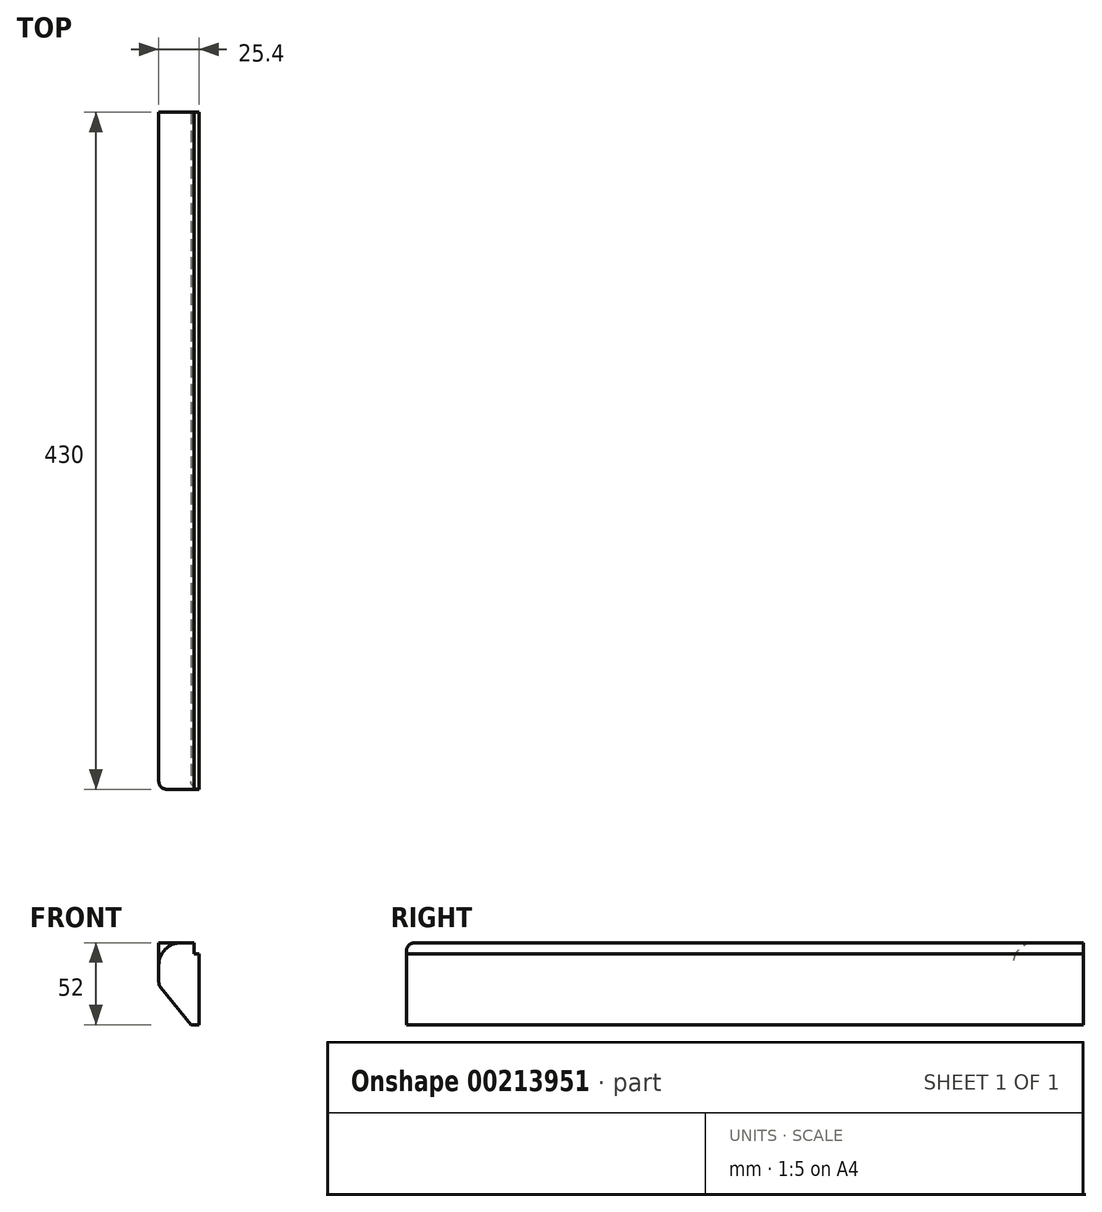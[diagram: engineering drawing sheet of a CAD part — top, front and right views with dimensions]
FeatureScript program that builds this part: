
annotation { "Feature Type Name" : "Feature", "Feature Type Description" : "" }
export const myFeature = defineFeature(function(context is Context, id is Id, definition is map)
    precondition{}
    {
        {
            var Q0;
            Q0=qCreatedBy(makeId("Front.planeOp"),FACE);
            var sketch = newSketch(context, id + "F0", { "sketchPlane" : qUnion([Q0])});
            skLineSegment(sketch, "E0.bottom", {"start": v(-25.49, -0.03) * mm, "end": v(-3.09, -0.03) * mm});
            skLineSegment(sketch, "E0.top", {"start": v(-5.09, -52.03) * mm, "end": v(-0.09, -52.03) * mm});
            skLineSegment(sketch, "E0.left", {"start": v(-25.49, -0.03) * mm, "end": v(-25.49, -25.25) * mm});
            skLineSegment(sketch, "E0.right", {"start": v(-0.09, -7.03) * mm, "end": v(-0.09, -52.03) * mm});
            skLineSegment(sketch, "E1", {"start": v(-24.36, -28.41) * mm, "end": v(-5.09, -52.03) * mm});
            skPoint(sketch, "E2.visualSharp", {"position": v(-25.49, -0.03) * mm});
            skPoint(sketch, "E3.visualSharp", {"position": v(-25.49, -27.03) * mm});
            skArc(sketch, "E3.filletArc", {"start": v(-25.49, -25.25) * mm, "mid": v(-25.2, -26.93) * mm, "end": v(-24.36, -28.41) * mm});
            skLineSegment(sketch, "E4.top", {"start": v(-3.09, -7.03) * mm, "end": v(-0.09, -7.03) * mm});
            skLineSegment(sketch, "E4.left", {"start": v(-3.09, -0.03) * mm, "end": v(-3.09, -7.03) * mm});
            skPoint(sketch, "E5.orphan", {"position": v(-0.09, -0.03) * mm});
            skSolve(sketch);
        }
        {
            var Q0;
            Q0 = qSketchRegion(id + "F0", true);
            extrude(context, id + "F1", {"entities" : qUnion([Q0]), "oppositeDirection" : true, "depth" : 430 * mm});
        }
        {
            var Q0;
            Q0=makeQuery(id+"F1.opExtrude","CAP_FACE",FACE,{"disambiguationData":[OSD([sQuery(id+"F0.wireOp",EDGE,"E0.bottom"),sQuery(id+"F0.wireOp",EDGE,"E0.top"),sQuery(id+"F0.wireOp",EDGE,"E0.left"),sQuery(id+"F0.wireOp",EDGE,"E0.right"),sQuery(id+"F0.wireOp",EDGE,"E1"),sQuery(id+"F0.wireOp",EDGE,"E3.filletArc")])],"isStart":false});
            cPlane(context, id + "F2", {"entities" : qUnion([Q0]), "cplaneType" : CPlaneType.OFFSET, "offset" : 45 * mm, "oppositeDirection" : true, "width" : 150 * mm, "height" : 150 * mm});
        }
        {
            var Q0;
            Q0=qCreatedBy(id+"F2.planeOp",FACE);
            var sketch = newSketch(context, id + "F3", { "sketchPlane" : qUnion([Q0])});
            skLineSegment(sketch, "E6.0", {"start": v(25.49, -0.03) * mm, "end": v(11.49, -0.03) * mm});
            skLineSegment(sketch, "E6.1", {"start": v(25.49, 3.94) * mm, "end": v(25.49, -14.03) * mm});
            skArc(sketch, "E7", {"start": v(25.49, -14.03) * mm, "mid": v(21.39, -4.13) * mm, "end": v(11.49, -0.03) * mm});
            skLineSegment(sketch, "E8", {"start": v(11.49, -0.03) * mm, "end": v(11.49, 3.94) * mm});
            skLineSegment(sketch, "E9", {"start": v(11.49, 3.94) * mm, "end": v(25.49, 3.94) * mm});
            skPoint(sketch, "E10.orphan", {"position": v(25.49, -25.25) * mm});
            skPoint(sketch, "E11.orphan", {"position": v(25.49, -0.03) * mm});
            skSolve(sketch);
        }
        {
            var Q0;
            Q0 = qSketchRegion(id + "F3", true);
            var Q1;
            Q1=sQuery(id+"F3.wireOp",EDGE,"E6.1");
            revolve(context, id + "F4", {"operationType" : NewBodyOperationType.REMOVE, "entities" : qUnion([Q0]), "axis" : qUnion([Q1]), "revolveType" : RevolveType.FULL, "oppositeDirection" : true});
        }
        {
            var Q0;
            Q0 = qSketchRegion(id + "F3", true);
            extrude(context, id + "F5", {"entities" : qUnion([Q0]), "operationType" : NewBodyOperationType.REMOVE, "endBound" : BoundingType.THROUGH_ALL, "oppositeDirection" : true, "depth" : 25 * mm});
        }
        {
            var Q0;
            Q0=makeQuery(id+"F1.opExtrude","CAP_EDGE",EDGE,{"disambiguationData":[OSD([sQuery(id+"F0.wireOp",EDGE,"E0.bottom")])],"isStart":true});
            fillet(context, id + "F6", {"entities" : qUnion([Q0]), "radius" : 5 * mm, "tangentPropagation" : true, "allowEdgeOverflow" : false});
        }
    });
